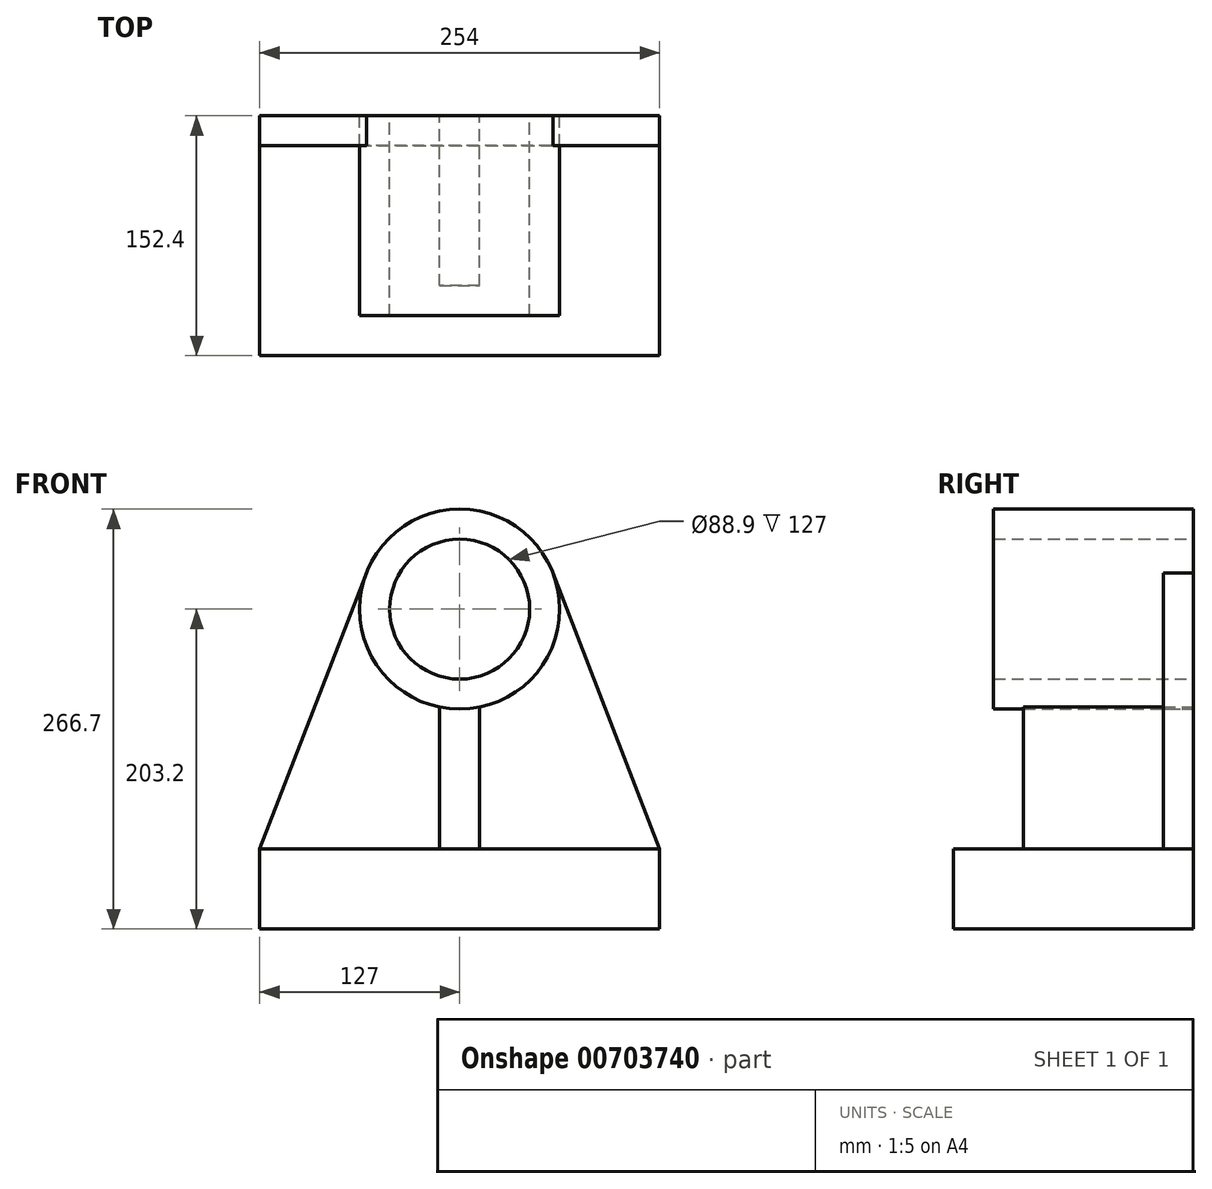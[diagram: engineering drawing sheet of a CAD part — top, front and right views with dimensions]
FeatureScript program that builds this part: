
annotation { "Feature Type Name" : "Feature", "Feature Type Description" : "" }
export const myFeature = defineFeature(function(context is Context, id is Id, definition is map)
    precondition{}
    {
        {
            var Q0;
            Q0=qCreatedBy(makeId("Front.planeOp"),FACE);
            var sketch = newSketch(context, id + "F0", { "sketchPlane" : qUnion([Q0])});
            skLineSegment(sketch, "E0.bottom", {"start": v(127, -25.4) * mm, "end": v(-127, -25.4) * mm});
            skLineSegment(sketch, "E0.top", {"start": v(127, 25.4) * mm, "end": v(-127, 25.4) * mm});
            skLineSegment(sketch, "E0.left", {"start": v(127, -25.4) * mm, "end": v(127, 25.4) * mm});
            skLineSegment(sketch, "E0.right", {"start": v(-127, -25.4) * mm, "end": v(-127, 25.4) * mm});
            skPoint(sketch, "E0.middle", {"position": v(0, 0) * mm});
            skCircle(sketch, "E1", {"center": v(0, 177.8) * mm, "radius": 63.5 * mm});
            skCircle(sketch, "E2", {"center": v(0, 177.8) * mm, "radius": 44.45 * mm});
            skLineSegment(sketch, "E3", {"start": v(127, 25.4) * mm, "end": v(62.71, 191.68) * mm});
            skLineSegment(sketch, "E4", {"start": v(-127, 25.4) * mm, "end": v(-66.25, 182.54) * mm});
            skLineSegment(sketch, "E5", {"start": v(-9.53, 25.4) * mm, "end": v(-9.53, 115.02) * mm});
            skLineSegment(sketch, "E6", {"start": v(9.53, 25.4) * mm, "end": v(9.53, 115.02) * mm});
            skSolve(sketch);
        }
        {
            var Q0;
            Q0=makeQuery(id+"F0.imprint","IMPRINT",FACE,{"disambiguationData":[TD([[makeQuery(id+"F0.imprint","IMPRINT",EDGE,{"derivedFrom":sQuery(id+"F0.wireOp",EDGE,"E0.bottom")}),-1.0]])]});
            extrude(context, id + "F1", {"entities" : qUnion([Q0]), "depth" : 152.4 * mm, "offsetDistance" : 25.4 * mm});
        }
        {
            var Q0;
            Q0=qCreatedBy(makeId("Front.planeOp"),FACE);
            var sketch = newSketch(context, id + "F2", { "sketchPlane" : qUnion([Q0])});
            skCircle(sketch, "E7", {"center": v(0, 177.8) * mm, "radius": 63.5 * mm});
            skCircle(sketch, "E8", {"center": v(0, 177.8) * mm, "radius": 44.45 * mm});
            skSolve(sketch);
        }
        {
            var Q0;
            Q0=qSketchRegion(id+"F2",true);
            extrude(context, id + "F3", {"entities" : qUnion([Q0]), "depth" : 127 * mm, "offsetDistance" : 25.4 * mm});
        }
        {
            var Q0;
            Q0=qCreatedBy(makeId("Front.planeOp"),FACE);
            var sketch = newSketch(context, id + "F4", { "sketchPlane" : qUnion([Q0])});
            skLineSegment(sketch, "E9", {"start": v(-12.7, 25.4) * mm, "end": v(-12.7, 115.58) * mm});
            skLineSegment(sketch, "E10", {"start": v(12.7, 25.4) * mm, "end": v(12.7, 115.58) * mm});
            skCircle(sketch, "E11.0", {"center": v(0, 177.8) * mm, "radius": 63.5 * mm});
            skLineSegment(sketch, "E12.0", {"start": v(152.4, 25.4) * mm, "end": v(-152.4, 25.4) * mm});
            skSolve(sketch);
        }
        {
            var Q0;
            {var subQ0=sQuery(id+"F4.wireOp",EDGE,"E9");Q0=makeQuery(id+"F4.imprint","IMPRINT",FACE,{"disambiguationData":[TD([[makeQuery(id+"F4.imprint","IMPRINT",EDGE,{"derivedFrom":subQ0}),-1.0]])]});}
            extrude(context, id + "F5", {"entities" : qUnion([Q0]), "depth" : 107.95 * mm, "offsetDistance" : 25.4 * mm});
        }
        {
            var Q0;
            Q0=qCreatedBy(makeId("Front.planeOp"),FACE);
            var sketch = newSketch(context, id + "F6", { "sketchPlane" : qUnion([Q0])});
            skCircle(sketch, "E13.0", {"center": v(0, 177.8) * mm, "radius": 63.5 * mm});
            skLineSegment(sketch, "E14.0", {"start": v(127, -25.4) * mm, "end": v(127, 25.4) * mm});
            skLineSegment(sketch, "E14.1", {"start": v(-127, -25.4) * mm, "end": v(127, -25.4) * mm});
            skLineSegment(sketch, "E14.2", {"start": v(-127, 25.4) * mm, "end": v(-127, -25.4) * mm});
            skLineSegment(sketch, "E14.3", {"start": v(127, 25.4) * mm, "end": v(-127, 25.4) * mm});
            skLineSegment(sketch, "E15", {"start": v(127, 25.4) * mm, "end": v(59.23, 200.7) * mm});
            skLineSegment(sketch, "E16", {"start": v(-127, 25.4) * mm, "end": v(-59.23, 200.7) * mm});
            skSolve(sketch);
        }
        {
            var Q0;
            Q0=makeQuery(id+"F6.imprint","IMPRINT",FACE,{"disambiguationData":[TD([[makeQuery(id+"F6.imprint","IMPRINT",EDGE,{"derivedFrom":sQuery(id+"F6.wireOp",EDGE,"E14.3")}),-1.0]])]});
            extrude(context, id + "F7", {"entities" : qUnion([Q0]), "depth" : 19.05 * mm, "offsetDistance" : 25.4 * mm});
        }
    });
